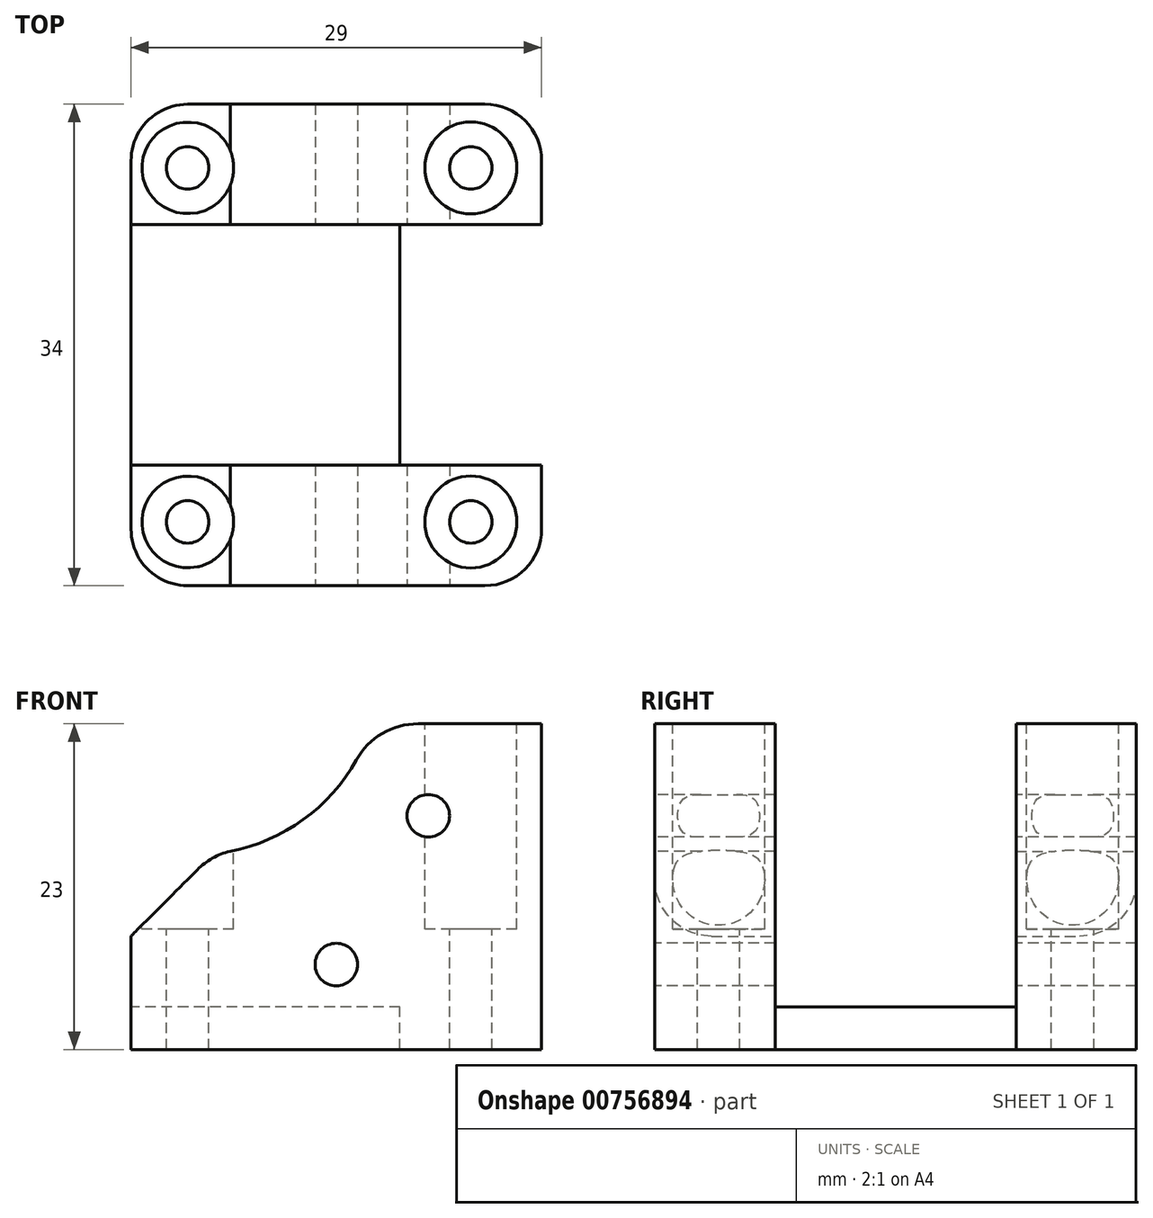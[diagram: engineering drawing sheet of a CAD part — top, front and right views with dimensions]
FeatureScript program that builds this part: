
annotation { "Feature Type Name" : "Feature", "Feature Type Description" : "" }
export const myFeature = defineFeature(function(context is Context, id is Id, definition is map)
    precondition{}
    {
        {
            var Q0;
            Q0=qCreatedBy(makeId("Front.planeOp"),FACE);
            var sketch = newSketch(context, id + "F0", { "sketchPlane" : qUnion([Q0])});
            skLineSegment(sketch, "E0.bottom", {"start": v(14.5, -1.5) * mm, "end": v(-14.5, -1.5) * mm});
            skLineSegment(sketch, "E0.top", {"start": v(14.5, 1.5) * mm, "end": v(-14.5, 1.5) * mm});
            skLineSegment(sketch, "E0.left", {"start": v(14.5, -1.5) * mm, "end": v(14.5, 1.5) * mm});
            skLineSegment(sketch, "E0.right", {"start": v(-14.5, -1.5) * mm, "end": v(-14.5, 1.5) * mm});
            skPoint(sketch, "E0.middle", {"position": v(0, 0) * mm});
            skSolve(sketch);
        }
        {
            var Q0;
            Q0=makeQuery(id+"F0.imprint","IMPRINT",FACE,{"disambiguationData":[TD([[makeQuery(id+"F0.imprint","IMPRINT",EDGE,{"derivedFrom":sQuery(id+"F0.wireOp",EDGE,"E0.bottom")}),-1.0]])]});
            extrude(context, id + "F1", {"entities" : qUnion([Q0]), "endBound" : BoundingType.SYMMETRIC, "depth" : 34 * mm, "offsetDistance" : 25 * mm});
        }
        {
            var Q0;
            Q0=makeQuery(id+"F1.opExtrude","CAP_FACE",FACE,{"disambiguationData":[OSD([sQuery(id+"F0.wireOp",EDGE,"E0.bottom"),sQuery(id+"F0.wireOp",EDGE,"E0.top"),sQuery(id+"F0.wireOp",EDGE,"E0.left"),sQuery(id+"F0.wireOp",EDGE,"E0.right")])],"isStart":false});
            var sketch = newSketch(context, id + "F2", { "sketchPlane" : qUnion([Q0])});
            skLineSegment(sketch, "E1", {"start": v(-14.5, 12.5) * mm, "end": v(-7.5, 12.5) * mm});
            skLineSegment(sketch, "E2", {"start": v(14.5, 1.5) * mm, "end": v(14.5, 21.5) * mm});
            skLineSegment(sketch, "E3", {"start": v(14.5, 21.5) * mm, "end": v(2.5, 21.5) * mm});
            skArc(sketch, "E4", {"start": v(2.5, 21.5) * mm, "mid": v(-1.25, 15.6) * mm, "end": v(-7.5, 12.5) * mm});
            skLineSegment(sketch, "E5", {"start": v(-14.5, 12.5) * mm, "end": v(-14.5, 1.5) * mm});
            skSolve(sketch);
        }
        {
            var Q0;
            Q0=makeQuery(id+"F2.imprint","IMPRINT",FACE,{"disambiguationData":[TD([[makeQuery(id+"F2.imprint","IMPRINT",EDGE,{"derivedFrom":sQuery(id+"F2.wireOp",EDGE,"E1")}),-1.0]])]});
            var Q1;
            Q1 = qSketchRegion(id + "F5", true);
            extrude(context, id + "F3", {"entities" : qUnion([Q0, Q1]), "depth" : 0 * mm, "offsetDistance" : 25 * mm, "hasSecondDirection" : true, "secondDirectionOppositeDirection" : true, "secondDirectionDepth" : 8.5 * mm});
        }
        {
            var Q0;
            Q0=makeQuery(id+"F3.opExtrude","SWEPT_BODY",BODY,{"disambiguationData":[OSD([sQuery(id+"F0.wireOp",EDGE,"E0.top"),sQuery(id+"F2.wireOp",EDGE,"E1"),sQuery(id+"F2.wireOp",EDGE,"E2"),sQuery(id+"F2.wireOp",EDGE,"E3"),sQuery(id+"F2.wireOp",EDGE,"6A3O42f3-pV0s-6iDU-mPt9-r4TsTGyD7GF8"),sQuery(id+"F2.wireOp",EDGE,"E4")])]});
            var Q1;
            Q1=qCreatedBy(makeId("Front.planeOp"),FACE);
            mirror(context, id + "F4", {"operationType" : NewBodyOperationType.ADD, "entities" : qUnion([Q0]), "mirrorPlane" : qUnion([Q1])});
        }
        {
            var Q0;
            Q0=makeQuery(id+"F1.opExtrude","SWEPT_FACE",FACE,{"disambiguationData":[OSD([sQuery(id+"F0.wireOp",EDGE,"E0.top")])]});
            var sketch = newSketch(context, id + "F5", { "sketchPlane" : qUnion([Q0])});
            skLineSegment(sketch, "E6.bottom", {"start": v(4.5, -8.5) * mm, "end": v(24.5, -8.5) * mm});
            skLineSegment(sketch, "E6.top", {"start": v(4.5, 8.5) * mm, "end": v(24.5, 8.5) * mm});
            skLineSegment(sketch, "E6.left", {"start": v(4.5, -8.5) * mm, "end": v(4.5, 8.5) * mm});
            skLineSegment(sketch, "E6.right", {"start": v(24.5, -8.5) * mm, "end": v(24.5, 8.5) * mm});
            skPoint(sketch, "E6.middle", {"position": v(14.5, 0) * mm});
            skSolve(sketch);
        }
        {
            var Q0;
            Q0 = qSketchRegion(id + "F5", true);
            var Q1;
            Q1=makeQuery(id+"F1.opExtrude","SWEPT_FACE",FACE,{"disambiguationData":[OSD([sQuery(id+"F0.wireOp",EDGE,"E0.bottom")])]});
            extrude(context, id + "F6", {"entities" : qUnion([Q0]), "operationType" : NewBodyOperationType.REMOVE, "endBound" : BoundingType.UP_TO_SURFACE, "oppositeDirection" : true, "depth" : 8.3 * mm, "endBoundEntityFace" : qUnion([Q1]), "offsetDistance" : 25 * mm});
        }
        {
            var Q0;
            Q0=makeQuery(id+"F3.opExtrude","SWEPT_FACE",FACE,{"disambiguationData":[OSD([sQuery(id+"F2.wireOp",EDGE,"E3")])]});
            var sketch = newSketch(context, id + "F7", { "sketchPlane" : qUnion([Q0])});
            skCircle(sketch, "E7", {"center": v(9.5, -12.5) * mm, "radius": 1.5 * mm});
            skCircle(sketch, "E8", {"center": v(9.5, 12.5) * mm, "radius": 1.5 * mm});
            skCircle(sketch, "E9", {"center": v(-10.5, 12.5) * mm, "radius": 1.5 * mm});
            skCircle(sketch, "E10", {"center": v(-10.5, -12.5) * mm, "radius": 1.5 * mm});
            skCircle(sketch, "E11", {"center": v(-10.5, 12.5) * mm, "radius": 3.25 * mm});
            skCircle(sketch, "E12", {"center": v(9.5, 12.5) * mm, "radius": 3.25 * mm});
            skCircle(sketch, "E13", {"center": v(9.5, -12.5) * mm, "radius": 3.25 * mm});
            skCircle(sketch, "E14", {"center": v(-10.5, -12.5) * mm, "radius": 3.25 * mm});
            skSolve(sketch);
        }
        {
            var Q0;
            Q0=makeQuery(id+"F7.imprint","IMPRINT",FACE,{"disambiguationData":[TD([[makeQuery(id+"F7.imprint","IMPRINT",EDGE,{"derivedFrom":sQuery(id+"F7.wireOp",EDGE,"E9")}),1.0]])]});
            var Q1;
            Q1=makeQuery(id+"F7.imprint","IMPRINT",FACE,{"disambiguationData":[TD([[makeQuery(id+"F7.imprint","IMPRINT",EDGE,{"derivedFrom":sQuery(id+"F7.wireOp",EDGE,"E10")}),1.0]])]});
            var Q2;
            Q2=makeQuery(id+"F7.imprint","IMPRINT",FACE,{"disambiguationData":[TD([[makeQuery(id+"F7.imprint","IMPRINT",EDGE,{"derivedFrom":sQuery(id+"F7.wireOp",EDGE,"E7")}),1.0]])]});
            var Q3;
            Q3=makeQuery(id+"F7.imprint","IMPRINT",FACE,{"disambiguationData":[TD([[makeQuery(id+"F7.imprint","IMPRINT",EDGE,{"derivedFrom":sQuery(id+"F7.wireOp",EDGE,"E8")}),1.0]])]});
            extrude(context, id + "F8", {"entities" : qUnion([Q0, Q1, Q2, Q3]), "operationType" : NewBodyOperationType.REMOVE, "endBound" : BoundingType.THROUGH_ALL, "oppositeDirection" : true, "depth" : 25 * mm, "offsetDistance" : 25 * mm});
        }
        {
            var Q0;
            Q0 = qSketchRegion(id + "F7", true);
            extrude(context, id + "F9", {"entities" : qUnion([Q0]), "operationType" : NewBodyOperationType.REMOVE, "oppositeDirection" : true, "depth" : 14.5 * mm, "offsetDistance" : 25 * mm});
        }
        {
            var Q0;
            {var subQ0=sQuery(id+"F0.wireOp",EDGE,"E0.top");Q0=makeQuery(id+"F4.boolean.opBoolean","MERGE",FACE,{"derivedFrom":[makeQuery(id+"F1.opExtrude","CAP_FACE",FACE,{"disambiguationData":[OSD([sQuery(id+"F0.wireOp",EDGE,"E0.bottom"),subQ0,sQuery(id+"F0.wireOp",EDGE,"E0.left"),sQuery(id+"F0.wireOp",EDGE,"E0.right")])],"isStart":false}),makeQuery(id+"F3.opExtrude","CAP_FACE",FACE,{"disambiguationData":[OSD([subQ0,sQuery(id+"F2.wireOp",EDGE,"E1"),sQuery(id+"F2.wireOp",EDGE,"E2"),sQuery(id+"F2.wireOp",EDGE,"E3"),sQuery(id+"F2.wireOp",EDGE,"6A3O42f3-pV0s-6iDU-mPt9-r4TsTGyD7GF8"),sQuery(id+"F2.wireOp",EDGE,"E4")])],"isStart":false})]});}
            var sketch = newSketch(context, id + "F10", { "sketchPlane" : qUnion([Q0])});
            skCircle(sketch, "E15", {"center": v(0, 4.5) * mm, "radius": 1.5 * mm});
            skCircle(sketch, "E16", {"center": v(6.5, 15) * mm, "radius": 1.5 * mm});
            skSolve(sketch);
        }
        {
            var Q0;
            Q0 = qSketchRegion(id + "F10", true);
            extrude(context, id + "F11", {"entities" : qUnion([Q0]), "operationType" : NewBodyOperationType.REMOVE, "endBound" : BoundingType.THROUGH_ALL, "oppositeDirection" : true, "depth" : 25 * mm, "offsetDistance" : 25 * mm});
        }
        {
            var Q0;
            Q0=makeQuery(id+"F3.opExtrude","SWEPT_EDGE",EDGE,{"disambiguationData":[OSD([sQuery(id+"F2.wireOp",EDGE,"E1"),sQuery(id+"F2.wireOp",EDGE,"E5")])]});
            var Q1;
            Q1=makeQuery(id+"F4.opPattern","COPY",EDGE,{"derivedFrom":makeQuery(id+"F3.opExtrude","SWEPT_EDGE",EDGE,{"disambiguationData":[OSD([sQuery(id+"F2.wireOp",EDGE,"E1"),sQuery(id+"F2.wireOp",EDGE,"E5")])]}),"instanceName":"1"});
            chamfer(context, id + "F12", {"entities" : qUnion([Q0, Q1]), "width" : 6 * mm, "tangentPropagation" : true});
        }
        {
            var Q0;
            Q0=makeQuery(id+"F1.opExtrude","CAP_EDGE",EDGE,{"disambiguationData":[OSD([sQuery(id+"F0.wireOp",EDGE,"E0.right")])],"isStart":false});
            var Q1;
            Q1=makeQuery(id+"F4.boolean.opBoolean","MERGE",EDGE,{"derivedFrom":[makeQuery(id+"F1.opExtrude","CAP_EDGE",EDGE,{"disambiguationData":[OSD([sQuery(id+"F0.wireOp",EDGE,"E0.left")])],"isStart":false}),makeQuery(id+"F3.opExtrude","CAP_EDGE",EDGE,{"disambiguationData":[OSD([sQuery(id+"F2.wireOp",EDGE,"E2")])],"isStart":false})]});
            var Q2;
            Q2=makeQuery(id+"F4.boolean.opBoolean","MERGE",EDGE,{"derivedFrom":[makeQuery(id+"F1.opExtrude","CAP_EDGE",EDGE,{"disambiguationData":[OSD([sQuery(id+"F0.wireOp",EDGE,"E0.left")])],"isStart":true}),makeQuery(id+"F4.opPattern","COPY",EDGE,{"derivedFrom":makeQuery(id+"F3.opExtrude","CAP_EDGE",EDGE,{"disambiguationData":[OSD([sQuery(id+"F2.wireOp",EDGE,"E2")])],"isStart":false}),"instanceName":"1"})]});
            var Q3;
            Q3=makeQuery(id+"F1.opExtrude","CAP_EDGE",EDGE,{"disambiguationData":[OSD([sQuery(id+"F0.wireOp",EDGE,"E0.right")])],"isStart":true});
            fillet(context, id + "F13", {"entities" : qUnion([Q0, Q1, Q2, Q3]), "radius" : 4 * mm, "tangentPropagation" : true, "allowEdgeOverflow" : false});
        }
        {
            var Q0;
            {var subQ0=sQuery(id+"F2.wireOp",EDGE,"E1");Q0=makeQuery(id+"F12.opChamfer","BLEND_EDGE",EDGE,{"disambiguationData":[OD(1.0)],"blendedFrom":[makeQuery(id+"F4.opPattern","COPY",EDGE,{"derivedFrom":makeQuery(id+"F3.opExtrude","SWEPT_EDGE",EDGE,{"disambiguationData":[OSD([subQ0,sQuery(id+"F2.wireOp",EDGE,"E5")])]}),"instanceName":"1"}),makeQuery(id+"F4.opPattern","COPY",FACE,{"derivedFrom":makeQuery(id+"F3.opExtrude","SWEPT_FACE",FACE,{"disambiguationData":[OSD([subQ0])]}),"instanceName":"1"})],"blendedInto":[makeQuery(id+"F4.opPattern","COPY",FACE,{"derivedFrom":makeQuery(id+"F3.opExtrude","SWEPT_FACE",FACE,{"disambiguationData":[OSD([subQ0])]}),"instanceName":"1"})]});}
            var Q1;
            Q1=makeQuery(id+"F4.opPattern","COPY",EDGE,{"derivedFrom":makeQuery(id+"F3.opExtrude","SWEPT_EDGE",EDGE,{"disambiguationData":[OSD([sQuery(id+"F2.wireOp",EDGE,"E3"),sQuery(id+"F2.wireOp",EDGE,"E4")])]}),"instanceName":"1"});
            var Q2;
            {var subQ0=sQuery(id+"F2.wireOp",EDGE,"E1");Q2=makeQuery(id+"F12.opChamfer","BLEND_EDGE",EDGE,{"disambiguationData":[OD(0.0)],"blendedFrom":[makeQuery(id+"F4.opPattern","COPY",EDGE,{"derivedFrom":makeQuery(id+"F3.opExtrude","SWEPT_EDGE",EDGE,{"disambiguationData":[OSD([subQ0,sQuery(id+"F2.wireOp",EDGE,"E5")])]}),"instanceName":"1"}),makeQuery(id+"F4.opPattern","COPY",FACE,{"derivedFrom":makeQuery(id+"F3.opExtrude","SWEPT_FACE",FACE,{"disambiguationData":[OSD([subQ0])]}),"instanceName":"1"})],"blendedInto":[makeQuery(id+"F4.opPattern","COPY",FACE,{"derivedFrom":makeQuery(id+"F3.opExtrude","SWEPT_FACE",FACE,{"disambiguationData":[OSD([subQ0])]}),"instanceName":"1"})]});}
            var Q3;
            Q3=makeQuery(id+"F3.opExtrude","SWEPT_EDGE",EDGE,{"disambiguationData":[OSD([sQuery(id+"F2.wireOp",EDGE,"E3"),sQuery(id+"F2.wireOp",EDGE,"E4")])]});
            var Q4;
            {var subQ0=sQuery(id+"F2.wireOp",EDGE,"E1");Q4=makeQuery(id+"F12.opChamfer","BLEND_EDGE",EDGE,{"disambiguationData":[OD(1.0)],"blendedFrom":[makeQuery(id+"F3.opExtrude","SWEPT_EDGE",EDGE,{"disambiguationData":[OSD([subQ0,sQuery(id+"F2.wireOp",EDGE,"E5")])]}),makeQuery(id+"F3.opExtrude","SWEPT_FACE",FACE,{"disambiguationData":[OSD([subQ0])]})],"blendedInto":[makeQuery(id+"F3.opExtrude","SWEPT_FACE",FACE,{"disambiguationData":[OSD([subQ0])]})]});}
            var Q5;
            {var subQ0=sQuery(id+"F2.wireOp",EDGE,"E1");Q5=makeQuery(id+"F12.opChamfer","BLEND_EDGE",EDGE,{"disambiguationData":[OD(0.0)],"blendedFrom":[makeQuery(id+"F3.opExtrude","SWEPT_EDGE",EDGE,{"disambiguationData":[OSD([subQ0,sQuery(id+"F2.wireOp",EDGE,"E5")])]}),makeQuery(id+"F3.opExtrude","SWEPT_FACE",FACE,{"disambiguationData":[OSD([subQ0])]})],"blendedInto":[makeQuery(id+"F3.opExtrude","SWEPT_FACE",FACE,{"disambiguationData":[OSD([subQ0])]})]});}
            fillet(context, id + "F14", {"entities" : qUnion([Q0, Q1, Q2, Q3, Q4, Q5]), "radius" : 5 * mm, "tangentPropagation" : true, "allowEdgeOverflow" : false});
        }
    });
